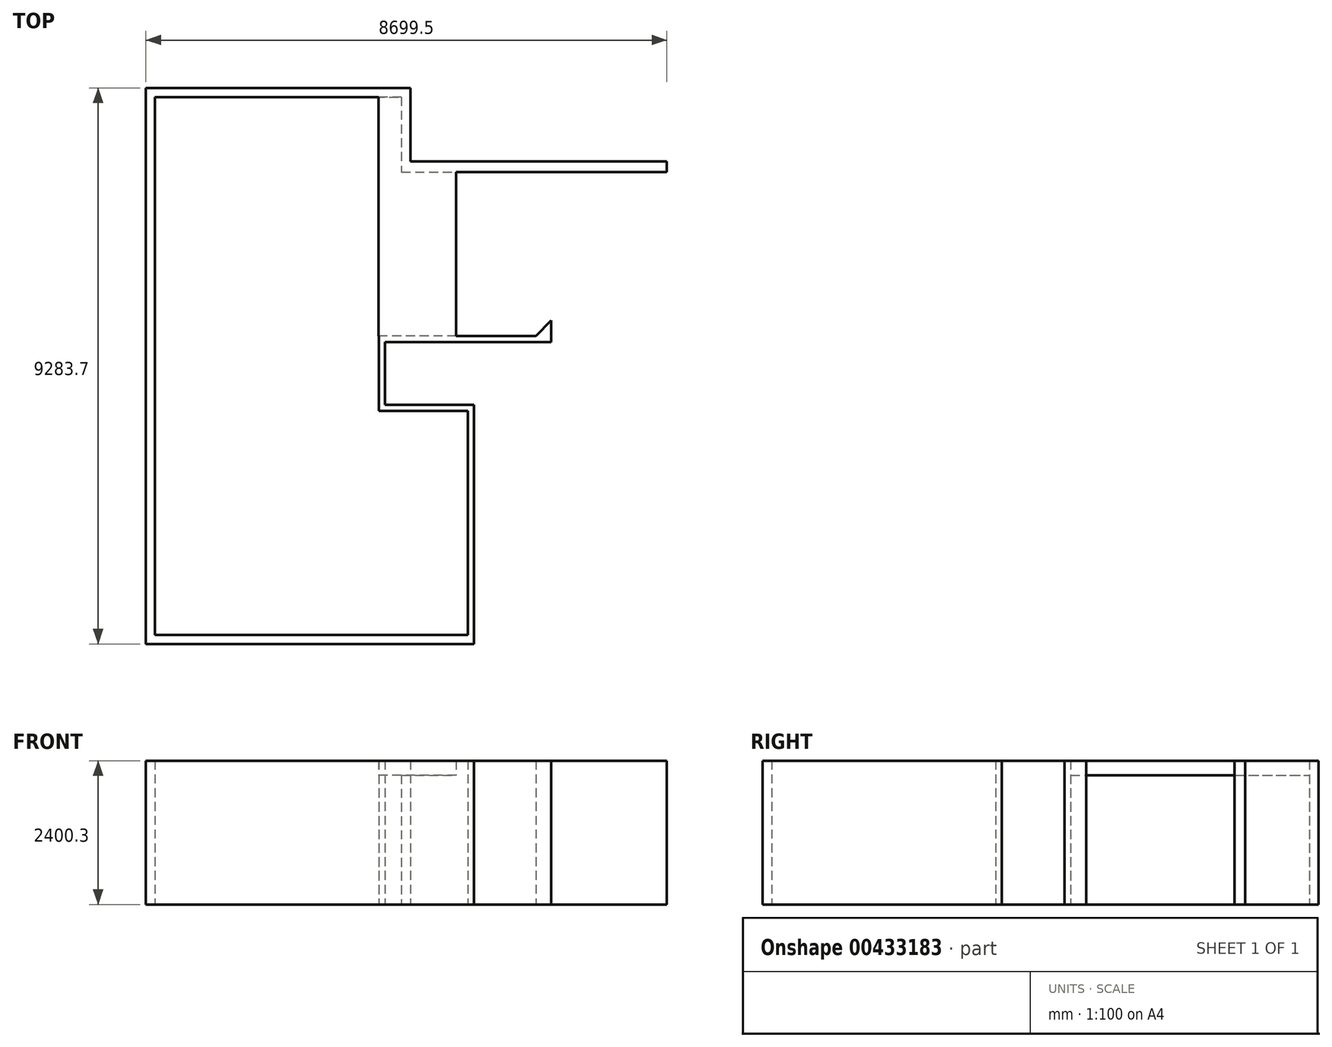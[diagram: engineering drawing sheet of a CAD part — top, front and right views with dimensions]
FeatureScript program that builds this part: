
annotation { "Feature Type Name" : "Feature", "Feature Type Description" : "" }
export const myFeature = defineFeature(function(context is Context, id is Id, definition is map)
    precondition{}
    {
        {
            var Q0;
            Q0=qCreatedBy(makeId("Top.planeOp"),FACE);
            var sketch = newSketch(context, id + "F0", { "sketchPlane" : qUnion([Q0])});
            skLineSegment(sketch, "E0", {"start": v(0, 0) * mm, "end": v(4114.8, 0) * mm});
            skLineSegment(sketch, "E1", {"start": v(4114.8, 0) * mm, "end": v(4114.8, -1225.55) * mm});
            skLineSegment(sketch, "E2", {"start": v(4114.8, -1225.55) * mm, "end": v(8547.1, -1225.55) * mm});
            skLineSegment(sketch, "E3", {"start": v(8547.1, -1225.55) * mm, "end": v(8547.1, -2139.95) * mm});
            skLineSegment(sketch, "E4", {"start": v(8547.1, -2139.95) * mm, "end": v(6616.7, -2139.95) * mm});
            skLineSegment(sketch, "E5", {"start": v(6616.7, -2139.95) * mm, "end": v(6616.7, -3729.17) * mm});
            skLineSegment(sketch, "E6", {"start": v(6358.07, -3987.8) * mm, "end": v(3740.15, -3987.8) * mm});
            skLineSegment(sketch, "E7", {"start": v(3740.15, -3987.8) * mm, "end": v(3740.15, -5238.75) * mm});
            skLineSegment(sketch, "E8", {"start": v(3740.15, -5238.75) * mm, "end": v(5226.05, -5238.75) * mm});
            skLineSegment(sketch, "E9", {"start": v(5226.05, -5238.75) * mm, "end": v(5226.05, -8978.9) * mm});
            skLineSegment(sketch, "E10", {"start": v(5226.05, -8978.9) * mm, "end": v(0, -8978.9) * mm});
            skLineSegment(sketch, "E11", {"start": v(0, -8978.9) * mm, "end": v(0, 0) * mm});
            skLineSegment(sketch, "E12", {"start": v(6616.7, -3729.17) * mm, "end": v(6358.07, -3987.8) * mm});
            skLineSegment(sketch, "E13.0", {"start": v(-152.4, 152.4) * mm, "end": v(4267.2, 152.4) * mm});
            skLineSegment(sketch, "E13.1", {"start": v(-152.4, -9131.3) * mm, "end": v(-152.4, 152.4) * mm});
            skLineSegment(sketch, "E13.2", {"start": v(5327.65, -9131.3) * mm, "end": v(-152.4, -9131.3) * mm});
            skLineSegment(sketch, "E14", {"start": v(6616.7, -3729.17) * mm, "end": v(6616.7, -4089.4) * mm});
            skLineSegment(sketch, "E15", {"start": v(6616.7, -4089.4) * mm, "end": v(3841.75, -4089.4) * mm});
            skLineSegment(sketch, "E16.0", {"start": v(5327.65, -5137.15) * mm, "end": v(5327.65, -9131.3) * mm});
            skLineSegment(sketch, "E16.1", {"start": v(3841.75, -5137.15) * mm, "end": v(5327.65, -5137.15) * mm});
            skLineSegment(sketch, "E16.2", {"start": v(3841.75, -4089.4) * mm, "end": v(3841.75, -5137.15) * mm});
            skLineSegment(sketch, "E17.0", {"start": v(4267.2, -1073.15) * mm, "end": v(8547.1, -1073.15) * mm});
            skLineSegment(sketch, "E17.1", {"start": v(4267.2, 152.4) * mm, "end": v(4267.2, -1073.15) * mm});
            skLineSegment(sketch, "E18", {"start": v(8547.1, -1073.15) * mm, "end": v(8547.1, -1225.55) * mm});
            skSolve(sketch);
        }
        {
            var Q0;
            Q0=makeQuery(id+"F0.imprint","IMPRINT",FACE,{"disambiguationData":[TD([[makeQuery(id+"F0.imprint","IMPRINT",EDGE,{"derivedFrom":sQuery(id+"F0.wireOp",EDGE,"E0")}),1.0]])]});
            extrude(context, id + "F1", {"entities" : qUnion([Q0]), "depth" : 2400.3 * mm});
        }
        {
            var Q0;
            Q0=qCreatedBy(makeId("Top.planeOp"),FACE);
            var sketch = newSketch(context, id + "F2", { "sketchPlane" : qUnion([Q0])});
            skLineSegment(sketch, "E19.bottom", {"start": v(800.1, -12.7) * mm, "end": v(2933.7, -12.7) * mm});
            skLineSegment(sketch, "E19.top", {"start": v(800.1, -444.5) * mm, "end": v(2933.7, -444.5) * mm});
            skLineSegment(sketch, "E19.left", {"start": v(800.1, -12.7) * mm, "end": v(800.1, -444.5) * mm});
            skLineSegment(sketch, "E19.right", {"start": v(2933.7, -12.7) * mm, "end": v(2933.7, -444.5) * mm});
            skSolve(sketch);
        }
        {
            var Q0;
            Q0=makeQuery(id+"F1.opExtrude","SWEPT_FACE",FACE,{"disambiguationData":[OSD([sQuery(id+"F0.wireOp",EDGE,"E0")])]});
            var sketch = newSketch(context, id + "F3", { "sketchPlane" : qUnion([Q0])});
            skLineSegment(sketch, "E20.bottom", {"start": v(4114.8, 2400.3) * mm, "end": v(3733.8, 2400.3) * mm});
            skLineSegment(sketch, "E20.top", {"start": v(4114.8, 2159) * mm, "end": v(3733.8, 2159) * mm});
            skLineSegment(sketch, "E20.left", {"start": v(4114.8, 2400.3) * mm, "end": v(4114.8, 2159) * mm});
            skLineSegment(sketch, "E20.right", {"start": v(3733.8, 2400.3) * mm, "end": v(3733.8, 2159) * mm});
            skSolve(sketch);
        }
        {
            var Q0;
            Q0=makeQuery(id+"F3.imprint","IMPRINT",FACE,{"disambiguationData":[TD([[makeQuery(id+"F3.imprint","IMPRINT",EDGE,{"derivedFrom":sQuery(id+"F3.wireOp",EDGE,"E20.bottom")}),-1.0]])]});
            var Q1;
            Q1=makeQuery(id+"F1.opExtrude","SWEPT_FACE",FACE,{"disambiguationData":[OSD([sQuery(id+"F0.wireOp",EDGE,"E6")])]});
            extrude(context, id + "F4", {"entities" : qUnion([Q0]), "endBound" : BoundingType.UP_TO_SURFACE, "endBoundEntityFace" : qUnion([Q1]), "depth" : 25.4 * mm});
        }
        {
            var Q0;
            Q0=makeQuery(id+"F1.opExtrude","SWEPT_FACE",FACE,{"disambiguationData":[OSD([sQuery(id+"F0.wireOp",EDGE,"E2")])]});
            extrude(context, id + "F5", {"entities" : qUnion([Q0]), "depth" : 25.4 * mm});
        }
        {
            var Q0;
            Q0=makeQuery(id+"F5.opExtrude","CAP_FACE",FACE,{"disambiguationData":[OSD([sQuery(id+"F0.wireOp",EDGE,"E2")])],"isStart":false});
            var sketch = newSketch(context, id + "F6", { "sketchPlane" : qUnion([Q0])});
            skLineSegment(sketch, "E21.bottom", {"start": v(4114.8, 2400.3) * mm, "end": v(5029.2, 2400.3) * mm});
            skLineSegment(sketch, "E21.top", {"start": v(4114.8, 2159) * mm, "end": v(5029.2, 2159) * mm});
            skLineSegment(sketch, "E21.left", {"start": v(4114.8, 2400.3) * mm, "end": v(4114.8, 2159) * mm});
            skLineSegment(sketch, "E21.right", {"start": v(5029.2, 2400.3) * mm, "end": v(5029.2, 2159) * mm});
            skSolve(sketch);
        }
        {
            var Q0;
            Q0=makeQuery(id+"F6.imprint","IMPRINT",FACE,{"disambiguationData":[TD([[makeQuery(id+"F6.imprint","IMPRINT",EDGE,{"derivedFrom":sQuery(id+"F6.wireOp",EDGE,"E21.bottom")}),-1.0]])]});
            var Q1;
            Q1=makeQuery(id+"F1.opExtrude","SWEPT_FACE",FACE,{"disambiguationData":[OSD([sQuery(id+"F0.wireOp",EDGE,"E6")])]});
            extrude(context, id + "F7", {"entities" : qUnion([Q0]), "operationType" : NewBodyOperationType.ADD, "endBound" : BoundingType.UP_TO_SURFACE, "endBoundEntityFace" : qUnion([Q1]), "depth" : 25.4 * mm});
        }
    });
